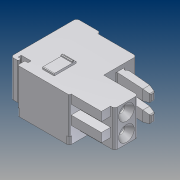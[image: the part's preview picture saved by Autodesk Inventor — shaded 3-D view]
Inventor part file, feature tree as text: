
AUTODESK INVENTOR PART (.ipt)
format: ipt  version: unknown  size: 427,008 bytes
history: native  units: mm (DEFAULTED — no unit token found)
features: sketch x20, extrude x19, pattern_linear x6, revolve x1
ambient origin geometry x8: Origin, YZ Plane, XZ Plane, XY Plane, X Axis, Y Axis, Z Axis, Center Point
feature tree (46):
  extrude  "Extrusion1"  Depth=1.5mm TaperAngle=0.0deg
  extrude  "Extrusion2"  Depth=1.5mm TaperAngle=0.0deg
  extrude  "Extrusion3"  Depth=1.5mm TaperAngle=0.0deg
  extrude  "Extrusion4"  Depth=1.5mm TaperAngle=0.0deg
  extrude  "Extrusion5"  TaperAngle=360.0deg  [1 undecoded]
  extrude  "Extrusion6"  Depth=3.3mm TaperAngle=0.0deg
  extrude  "Extrusion7"  Depth=1.0mm TaperAngle=0.0deg
  extrude  "Extrusion8"  Depth=1.0mm TaperAngle=0.0deg
  extrude  "Extrusion9"  Depth=0.9mm TaperAngle=0.0deg
  revolve  "Revolution1"  [1 undecoded]
  pattern_linear  "Rectangular Pattern1"  Count1=2 Spacing1=3.5mm
  extrude  "Extrusion10"  Depth=20.0mm TaperAngle=0.0deg
  pattern_linear  "Rectangular Pattern2"  [2 undecoded]
  extrude  "Extrusion11"  [1 undecoded]
  pattern_linear  "Rectangular Pattern3"  [2 undecoded]
  extrude  "Extrusion12"  [1 undecoded]
  pattern_linear  "Rectangular Pattern4"  [2 undecoded]
  extrude  "Extrusion13"  [1 undecoded]
  extrude  "Extrusion14"  [1 undecoded]
  extrude  "Extrusion15"  [1 undecoded]
  extrude  "Extrusion16"  [1 undecoded]
  extrude  "Extrusion17"  [1 undecoded]
  pattern_linear  "Rectangular Pattern5"  [2 undecoded]
  extrude  "Extrusion18"  [1 undecoded]
  pattern_linear  "Rectangular Pattern6"  [2 undecoded]
  extrude  "Extrusion19"  [1 undecoded]
  sketch  "Skizze_1"  dims[d0=7.0mm d1=0.0mm d2=1.5mm d3=0.0mm]
  sketch  "Skizze_3"  dims[d8=1.5mm d9=0.0mm d10=1.5mm d11=0.0mm]
  sketch  "Skizze_4"  dims[d12=1.5mm d13=0.0mm d14=1.5mm d15=0.0mm]
  sketch  "Skizze_5"  dims[d16=1.4mm d17=0.0mm d18=360.0deg]
  sketch  "Skizze_6"  dims[d19=20.0mm d21=3.5mm d22=10.0mm d24=0.0mm d25=3.3mm d26=0.0mm]
  sketch  "Skizze_7"  dims[d27=20.0mm d29=3.5mm d30=10.0mm d32=0.0mm d33=1.0mm d34=0.0mm]
  sketch  "Skizze_8"  dims[d35=20.0mm d37=3.5mm d38=10.0mm d40=0.0mm d41=1.0mm d42=0.0mm]
  sketch  "Skizze_9"  dims[d43=20.0mm d45=3.5mm d46=10.0mm d48=0.0mm d49=0.9mm d50=0.0mm]
  sketch  "Skizze_2"  dims[d4=1.5mm d5=0.0mm d6=1.5mm d7=0.0mm]
  sketch  "Skizze_10"  dims[d51=0.9mm d52=0.0mm d53=1.7mm d54=0.0mm]
  sketch  "Skizze_12"  dims[d55=1.7mm d56=0.0mm]
  sketch  "Skizze_14"  dims[d57=2.0mm d58=0.0mm d59=20.0mm d61=3.5mm d62=10.0mm d64=0.0mm]
  sketch  "Skizze_16"  dims[d65=1.7mm d66=0.0mm d67=20.0mm d69=3.5mm d70=10.0mm d72=0.0mm]
  sketch  "Skizze_18"  dims[d73=2.2mm d74=0.0mm]
  sketch  "Skizze_19"
  sketch  "Skizze_20"
  sketch  "Skizze_21"
  sketch  "Skizze_22"
  sketch  "Skizze_24"
  sketch  "Skizze_26"
note: 21 required parameter values undecoded (feature->parameter linkage not recoverable at this tier; creation-order binding heuristic only, values carry confidence <= 0.55)